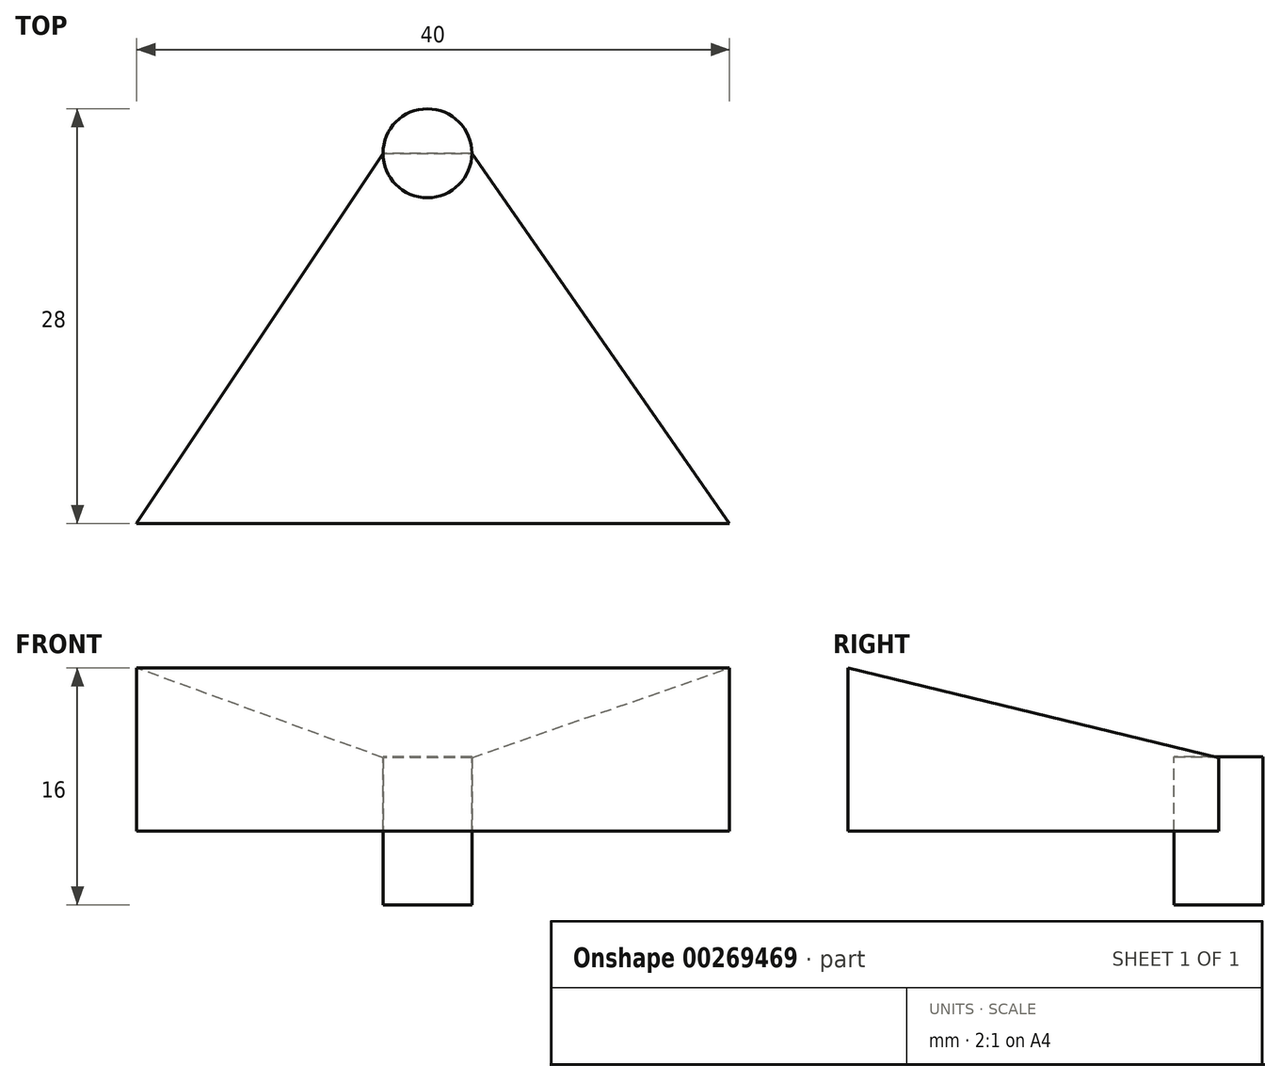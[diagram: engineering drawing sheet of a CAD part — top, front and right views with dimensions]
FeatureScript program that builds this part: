
annotation { "Feature Type Name" : "Feature", "Feature Type Description" : "" }
export const myFeature = defineFeature(function(context is Context, id is Id, definition is map)
    precondition{}
    {
        {
            var Q0;
            Q0=qCreatedBy(makeId("Top.planeOp"),FACE);
            var sketch = newSketch(context, id + "F0", { "sketchPlane" : qUnion([Q0])});
            skCircle(sketch, "E0", {"center": v(0, 0) * mm, "radius": 3 * mm});
            skSolve(sketch);
        }
        {
            var Q0;
            Q0=makeQuery(id+"F0.imprint","IMPRINT",FACE,{"disambiguationData":[TD([[makeQuery(id+"F0.imprint","IMPRINT",EDGE,{"derivedFrom":sQuery(id+"F0.wireOp",EDGE,"E0")}),1.0]])]});
            extrude(context, id + "F1", {"entities" : qUnion([Q0]), "endBound" : BoundingType.SYMMETRIC, "oppositeDirection" : true, "depth" : 10 * mm});
        }
        {
            var Q0;
            Q0=qCreatedBy(makeId("Front.planeOp"),FACE);
            var sketch = newSketch(context, id + "F2", { "sketchPlane" : qUnion([Q0])});
            skLineSegment(sketch, "E1.bottom", {"start": v(-19.62, 0) * mm, "end": v(20.38, 0) * mm});
            skLineSegment(sketch, "E1.top", {"start": v(-19.62, 11) * mm, "end": v(20.38, 11) * mm});
            skLineSegment(sketch, "E1.left", {"start": v(-19.62, 0) * mm, "end": v(-19.62, 11) * mm});
            skLineSegment(sketch, "E1.right", {"start": v(20.38, 0) * mm, "end": v(20.38, 11) * mm});
            skSolve(sketch);
        }
        {
            var Q0;
            Q0=makeQuery(id+"F2.imprint","IMPRINT",FACE,{"disambiguationData":[TD([[makeQuery(id+"F2.imprint","IMPRINT",EDGE,{"derivedFrom":sQuery(id+"F2.wireOp",EDGE,"E1.bottom")}),1.0]])]});
            extrude(context, id + "F3", {"entities" : qUnion([Q0]), "depth" : 25 * mm});
        }
        {
            var Q0;
            Q0=qCreatedBy(makeId("Top.planeOp"),FACE);
            var sketch = newSketch(context, id + "F4", { "sketchPlane" : qUnion([Q0])});
            skLineSegment(sketch, "E2", {"start": v(-3, 0) * mm, "end": v(-19.94, -25.45) * mm});
            skLineSegment(sketch, "E3", {"start": v(-19.94, -25.45) * mm, "end": v(-27, 2.68) * mm});
            skLineSegment(sketch, "E4", {"start": v(-27, 2.68) * mm, "end": v(-3, 0) * mm});
            skLineSegment(sketch, "E5", {"start": v(3, 0) * mm, "end": v(20.7, -25.45) * mm});
            skLineSegment(sketch, "E6", {"start": v(20.7, -25.45) * mm, "end": v(32.64, 2.68) * mm});
            skLineSegment(sketch, "E7", {"start": v(32.64, 2.68) * mm, "end": v(3, 0) * mm});
            skSolve(sketch);
        }
        {
            var Q0;
            Q0 = qSketchRegion(id + "F4", true);
            extrude(context, id + "F5", {"entities" : qUnion([Q0]), "operationType" : NewBodyOperationType.REMOVE, "endBound" : BoundingType.THROUGH_ALL, "depth" : 25 * mm});
        }
        {
            var Q0;
            Q0=qCreatedBy(makeId("Right.planeOp"),FACE);
            var sketch = newSketch(context, id + "F6", { "sketchPlane" : qUnion([Q0])});
            skLineSegment(sketch, "E8", {"start": v(-25.72, 11.17) * mm, "end": v(6.2, 3.44) * mm});
            skLineSegment(sketch, "E9", {"start": v(6.2, 3.44) * mm, "end": v(6.2, 13.68) * mm});
            skLineSegment(sketch, "E10", {"start": v(6.2, 13.68) * mm, "end": v(-25.72, 11.17) * mm});
            skSolve(sketch);
        }
        {
            var Q0;
            Q0 = qSketchRegion(id + "F6", true);
            extrude(context, id + "F7", {"entities" : qUnion([Q0]), "endBound" : BoundingType.SYMMETRIC, "depth" : 50 * mm});
        }
        {
            var Q0;
            Q0=makeQuery(id+"F7.opExtrude","SWEPT_BODY",BODY,{"disambiguationData":[OSD([sQuery(id+"F6.wireOp",EDGE,"E8"),sQuery(id+"F6.wireOp",EDGE,"E9"),sQuery(id+"F6.wireOp",EDGE,"E10")])]});
            var Q1;
            Q1=makeQuery(id+"F3.opExtrude","SWEPT_BODY",BODY,{"disambiguationData":[OSD([sQuery(id+"F2.wireOp",EDGE,"E1.bottom"),sQuery(id+"F2.wireOp",EDGE,"E1.top"),sQuery(id+"F2.wireOp",EDGE,"E1.left"),sQuery(id+"F2.wireOp",EDGE,"E1.right")])]});
            booleanBodies(context, id + "F8", {"operationType" : BooleanOperationType.SUBTRACTION, "tools" : qUnion([Q0]), "targets" : qUnion([Q1])});
        }
    });
